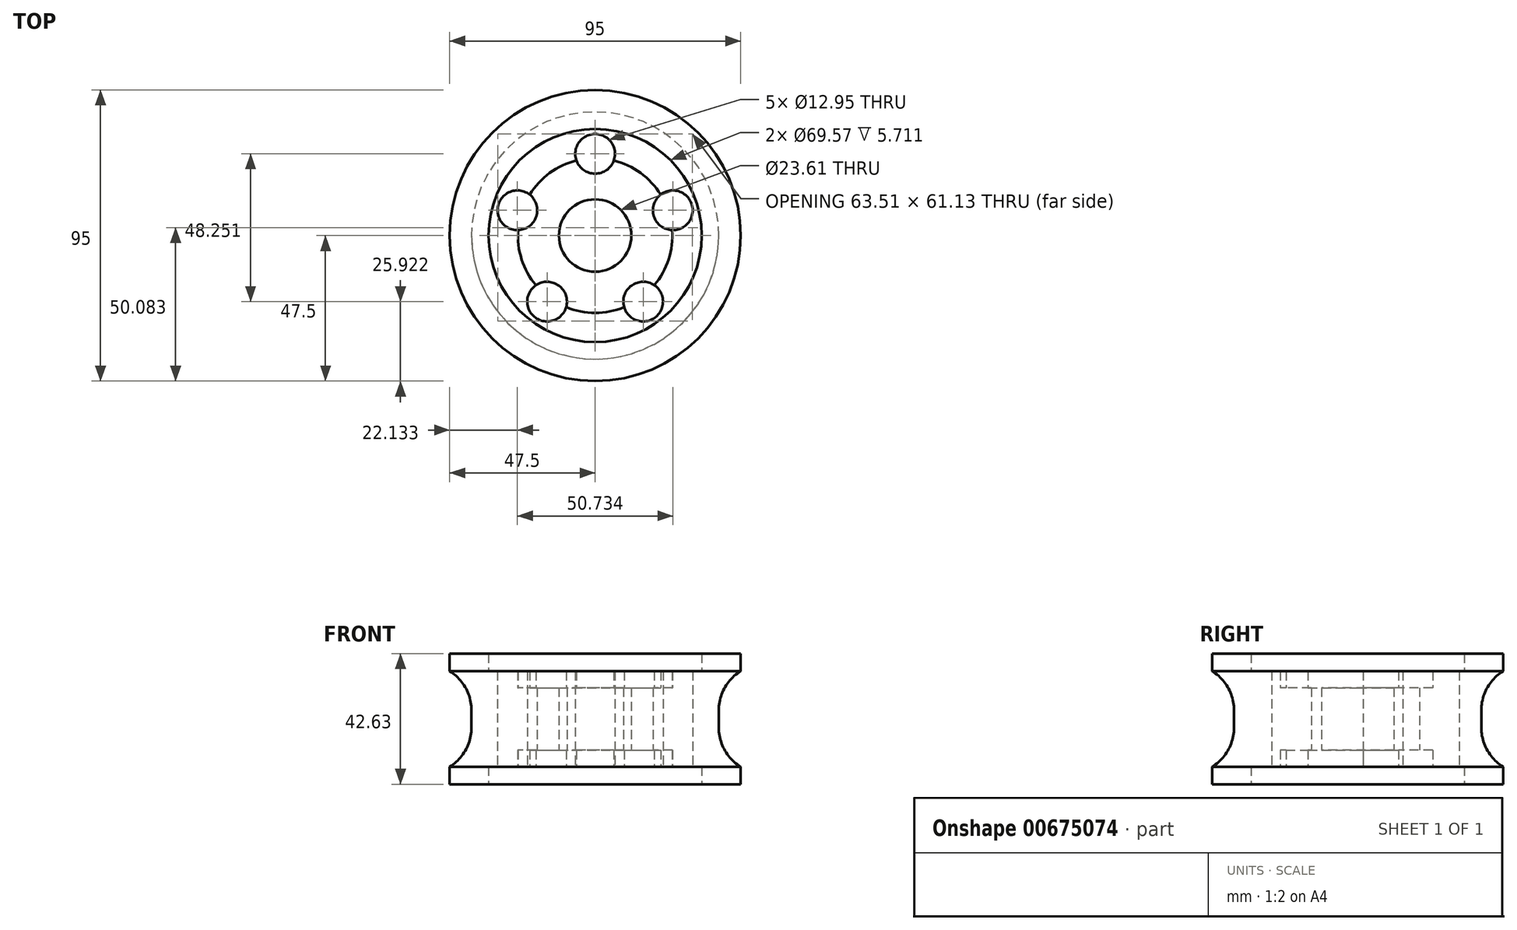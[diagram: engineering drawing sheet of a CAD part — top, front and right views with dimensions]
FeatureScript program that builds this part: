
annotation { "Feature Type Name" : "Feature", "Feature Type Description" : "" }
export const myFeature = defineFeature(function(context is Context, id is Id, definition is map)
    precondition{}
    {
        {
            var Q0;
            Q0=qCreatedBy(makeId("Front.planeOp"),FACE);
            var sketch = newSketch(context, id + "F0", { "sketchPlane" : qUnion([Q0])});
            skLineSegment(sketch, "E0", {"start": v(-59.21, 21.31) * mm, "end": v(0, 21.31) * mm, "construction": true});
            skLineSegment(sketch, "E1", {"start": v(-11.8, 21.31) * mm, "end": v(-11.8, 31.5) * mm});
            skLineSegment(sketch, "E2", {"start": v(-11.8, 31.5) * mm, "end": v(-25.23, 31.5) * mm});
            skLineSegment(sketch, "E3", {"start": v(-25.23, 31.5) * mm, "end": v(-25.23, 36.92) * mm});
            skLineSegment(sketch, "E4", {"start": v(-25.23, 36.92) * mm, "end": v(-34.78, 36.92) * mm});
            skLineSegment(sketch, "E5", {"start": v(-34.78, 36.92) * mm, "end": v(-34.78, 42.63) * mm});
            skLineSegment(sketch, "E6", {"start": v(-34.78, 42.63) * mm, "end": v(-47.5, 42.63) * mm});
            skLineSegment(sketch, "E7", {"start": v(-47.5, 42.63) * mm, "end": v(-47.5, 36.92) * mm});
            skLineSegment(sketch, "E8", {"start": v(-47.5, 36.92) * mm, "end": v(-40.36, 36.92) * mm});
            skLineSegment(sketch, "E9", {"start": v(-40.36, 36.92) * mm, "end": v(-40.36, 21.31) * mm});
            skLineSegment(sketch, "E10.MirrorCS", {"start": v(-47.5, 0) * mm, "end": v(-47.5, 5.71) * mm});
            skLineSegment(sketch, "E11.MirrorCS", {"start": v(-25.23, 11.14) * mm, "end": v(-25.23, 5.71) * mm});
            skLineSegment(sketch, "E12.MirrorCS", {"start": v(-47.5, 5.71) * mm, "end": v(-40.36, 5.71) * mm});
            skLineSegment(sketch, "E13.MirrorCS", {"start": v(-34.78, 5.71) * mm, "end": v(-34.78, 0) * mm});
            skLineSegment(sketch, "E14.MirrorCS", {"start": v(-11.8, 21.31) * mm, "end": v(-11.8, 11.14) * mm});
            skLineSegment(sketch, "E15.MirrorCS", {"start": v(-11.8, 11.14) * mm, "end": v(-25.23, 11.14) * mm});
            skLineSegment(sketch, "E16.MirrorCS", {"start": v(-34.78, 0) * mm, "end": v(-47.5, 0) * mm});
            skLineSegment(sketch, "E17.MirrorCS", {"start": v(-25.23, 5.71) * mm, "end": v(-34.78, 5.71) * mm});
            skLineSegment(sketch, "E18.MirrorCS", {"start": v(-40.36, 5.71) * mm, "end": v(-40.36, 21.31) * mm});
            skLineSegment(sketch, "E19", {"start": v(0, 21.31) * mm, "end": v(0, 58.83) * mm, "construction": true});
            skLineSegment(sketch, "E20", {"start": v(-34.78, 0) * mm, "end": v(0, 0) * mm, "construction": true});
            skLineSegment(sketch, "E21", {"start": v(-103.61, 85.98) * mm, "end": v(-106.48, 90.93) * mm, "construction": true});
            skSolve(sketch);
        }
        {
            var Q0;
            Q0=makeQuery(id+"F0.imprint","IMPRINT",FACE,{"disambiguationData":[TD([[makeQuery(id+"F0.imprint","IMPRINT",EDGE,{"derivedFrom":sQuery(id+"F0.wireOp",EDGE,"E1")}),1.0]])]});
            var Q1;
            Q1=sQuery(id+"F0.wireOp",EDGE,"E19");
            revolve(context, id + "F1", {"entities" : qUnion([Q0]), "axis" : qUnion([Q1]), "revolveType" : RevolveType.FULL});
        }
        {
            var Q0;
            Q0=makeQuery(id+"F1.opRevolve","SWEPT_FACE",FACE,{"disambiguationData":[OSD([sQuery(id+"F0.wireOp",EDGE,"E9"),sQuery(id+"F0.wireOp",EDGE,"E18.MirrorCS")])]});
            fillet(context, id + "F2", {"entities" : qUnion([Q0]), "radius" : 15 * mm, "tangentPropagation" : true, "allowEdgeOverflow" : false});
        }
        {
            var Q0;
            Q0=qCreatedBy(makeId("Top.planeOp"),FACE);
            var sketch = newSketch(context, id + "F3", { "sketchPlane" : qUnion([Q0])});
            skCircle(sketch, "E22", {"center": v(0, 0) * mm, "radius": 33.34 * mm, "construction": true});
            skCircle(sketch, "E23", {"center": v(0, 0) * mm, "radius": 20 * mm, "construction": true});
            skLineSegment(sketch, "E24", {"start": v(0, 20) * mm, "end": v(0, 33.34) * mm, "construction": true});
            skCircle(sketch, "E25", {"center": v(0, 26.67) * mm, "radius": 6.48 * mm});
            skCircle(sketch, "E26.1.0", {"center": v(-25.37, 8.24) * mm, "radius": 6.48 * mm});
            skCircle(sketch, "E26.2.0", {"center": v(-15.68, -21.58) * mm, "radius": 6.48 * mm});
            skCircle(sketch, "E26.3.0", {"center": v(15.68, -21.58) * mm, "radius": 6.48 * mm});
            skCircle(sketch, "E26.4.0", {"center": v(25.37, 8.24) * mm, "radius": 6.48 * mm});
            skSolve(sketch);
        }
        {
            var Q0;
            Q0=makeQuery(id+"F1.opRevolve","SWEPT_FACE",FACE,{"disambiguationData":[OSD([sQuery(id+"F0.wireOp",EDGE,"E4")])]});
            var Q1;
            Q1 = qSketchRegion(id + "F3", true);
            extrude(context, id + "F4", {"entities" : qUnion([Q0, Q1]), "operationType" : NewBodyOperationType.REMOVE, "depth" : 236.4 * mm, "offsetDistance" : 25 * mm});
        }
    });
